# Revit family: led_hc350_22w_dim_4000k_ip44_apollo_520021000800
name_source: partatom
category: Leuchten
revit_build: Autodesk Revit 2016 (Build: 20190508_0715(x64)
units: mm (PartAtom-declared; Revit-internal decimal feet)

## family parameters
Basisbauteil = Fläche
Beim Laden mit Abzugskörper schneiden = Nein
Bemaßung runder Anschluss = Durchmesser verwenden
Gemeinsam genutzt = Nein
Lichtquelle = Nein
Raumberechnungspunkt = Nein
Teiletyp = Normal

## types (1)
- LED HC350 22W DIM 4000K IP44 Apollo (1 x LED, 2040 lm)
    Approval mark = CE
    Beschreibung = Professional wall/ceiling luminaire with comfortable diffused light. Easy installation on wall or ceiling. Bracket accessory available for easy mounting on existing installations (no new screw holes needed). Module Clio inside. Uniform, diffused light, creating a pleasant atmosphere. IP44 versions also suitable for bathrooms and comparable spaces. Energy saving up to 80% in comparison to a traditional light source.
    CIE Flux Codes = 38 68 88 85 100
    Control Gear = Electronic ballast
    Height = 110 mm
    Hersteller = OPPLE
    Lamp Light Flux = 2040 lm
    Lamp count = 1
    Lampe = 1 x LED
    Length = 337 mm
    Luminous efficacy = 93 lm/W
    ModVariant = Nein
    Modell = 520021000800
    Mounting Place = Ceiling, Wall
    Mounting Type = Surface mounted
    Number of Poles = 1
    OnlyDefault = Ja
    Power Factor = 1
    Product Name = LED HC350 22W DIM 4000K IP44 Apollo
    Product group = Ceiling Light Apollo
    ProductGroupID = 301
    Protection Class = Protection class I
    Protection Degree = IP 44
    RLX_Detail_Level = 1
    RlxData = <blob elided: 81429 chars, md5=f74a303e>
    Scheinlast = 22 VA
    Socket = socket
    Standby Power = 0 W
    System Light Flux = 2040 lm
    System Power = 22 W
    Typenbild = 520021000800.jpg
    Typenkommentare = Product without accessories
    URL = http://relux.com
    VarID = ---
    Voltage = 0 V
    Vorgabe-Ansicht = 1800 mm
    Weight = 0.00 kg
    Width = 0 mm  [stored 0 ft]

note: [stored X ft] marks values corroborated as IEEE doubles in the binary element streams (Revit-internal decimal feet)

## geometry (parser evidence)
native form markers: Blend x4, Sweep x8
no freeform markers — native parametric forms only
